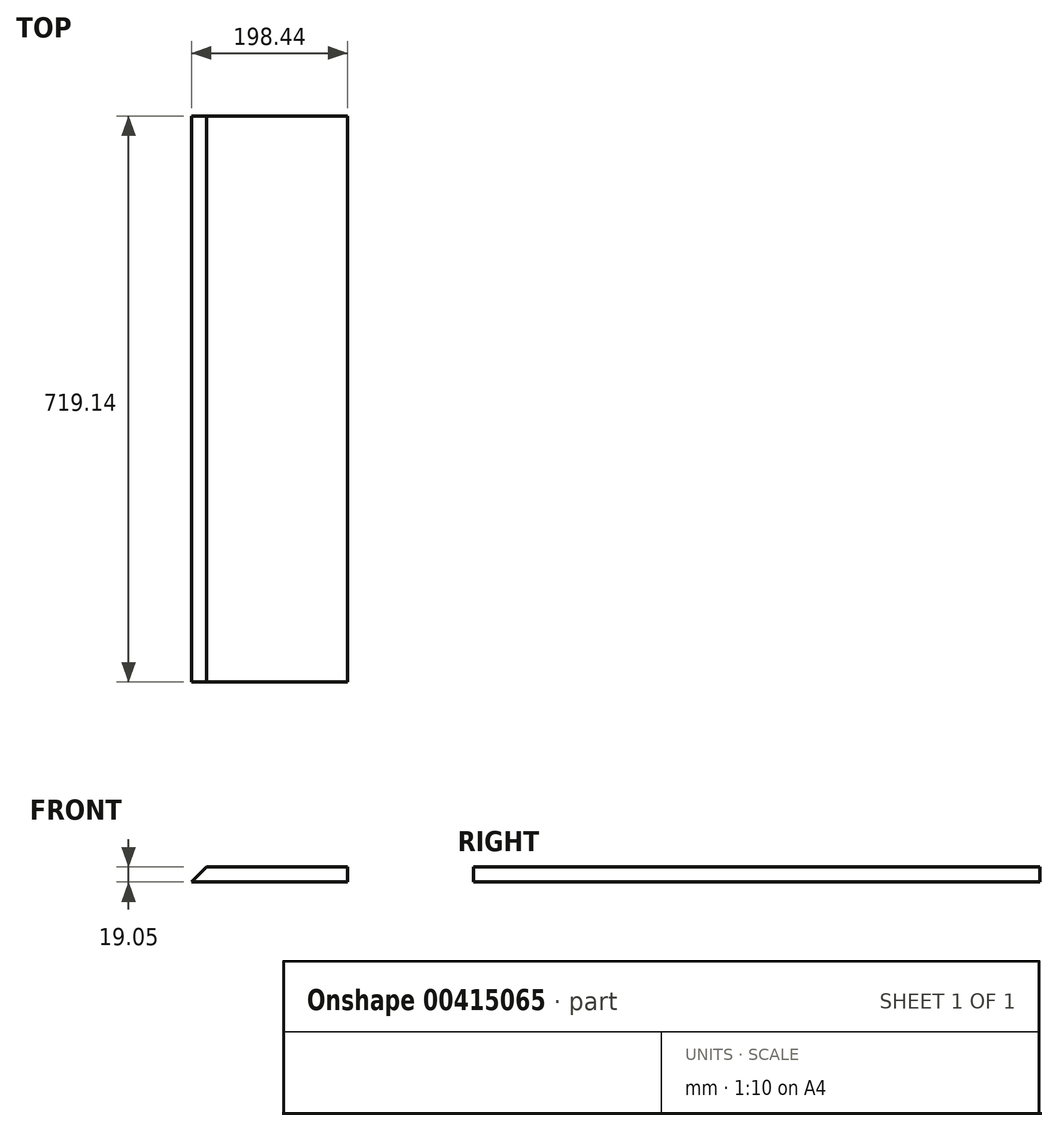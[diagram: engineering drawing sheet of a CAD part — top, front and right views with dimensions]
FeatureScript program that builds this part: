
annotation { "Feature Type Name" : "Feature", "Feature Type Description" : "" }
export const myFeature = defineFeature(function(context is Context, id is Id, definition is map)
    precondition{}
    {
        {
            var Q0;
            Q0=qCreatedBy(makeId("Front.planeOp"),FACE);
            var sketch = newSketch(context, id + "F0", { "sketchPlane" : qUnion([Q0])});
            skLineSegment(sketch, "E0.bottom", {"start": v(0, 0) * mm, "end": v(198.44, 0) * mm});
            skLineSegment(sketch, "E0.top", {"start": v(0, 19.05) * mm, "end": v(198.44, 19.05) * mm});
            skLineSegment(sketch, "E0.left", {"start": v(0, 0) * mm, "end": v(0, 19.05) * mm});
            skLineSegment(sketch, "E0.right", {"start": v(198.44, 0) * mm, "end": v(198.44, 19.05) * mm});
            skSolve(sketch);
        }
        {
            var Q0;
            Q0=makeQuery(id+"F0.imprint","IMPRINT",FACE,{"disambiguationData":[TD([[makeQuery(id+"F0.imprint","IMPRINT",EDGE,{"derivedFrom":sQuery(id+"F0.wireOp",EDGE,"E0.bottom")}),1.0]])]});
            extrude(context, id + "F1", {"entities" : qUnion([Q0]), "depth" : 719.14 * mm, "offsetDistance" : 25.4 * mm});
        }
        {
            var Q0;
            Q0=makeQuery(id+"F1.opExtrude","CAP_FACE",FACE,{"disambiguationData":[OSD([sQuery(id+"F0.wireOp",EDGE,"E0.bottom"),sQuery(id+"F0.wireOp",EDGE,"E0.top"),sQuery(id+"F0.wireOp",EDGE,"E0.left"),sQuery(id+"F0.wireOp",EDGE,"E0.right")])],"isStart":false});
            var sketch = newSketch(context, id + "F2", { "sketchPlane" : qUnion([Q0])});
            skLineSegment(sketch, "E1", {"start": v(0, 0) * mm, "end": v(19.05, 19.05) * mm});
            skSolve(sketch);
        }
        {
            var Q0;
            {var subQ0=sQuery(id+"F2.wireOp",EDGE,"E1");Q0=makeQuery(id+"F2.imprint","IMPRINT",FACE,{"disambiguationData":[TD([[makeQuery(id+"F2.imprint","IMPRINT",EDGE,{"derivedFrom":subQ0}),1.0]])]});}
            extrude(context, id + "F3", {"entities" : qUnion([Q0]), "operationType" : NewBodyOperationType.REMOVE, "endBound" : BoundingType.THROUGH_ALL, "oppositeDirection" : true, "depth" : 25.4 * mm, "offsetDistance" : 25.4 * mm});
        }
    });
